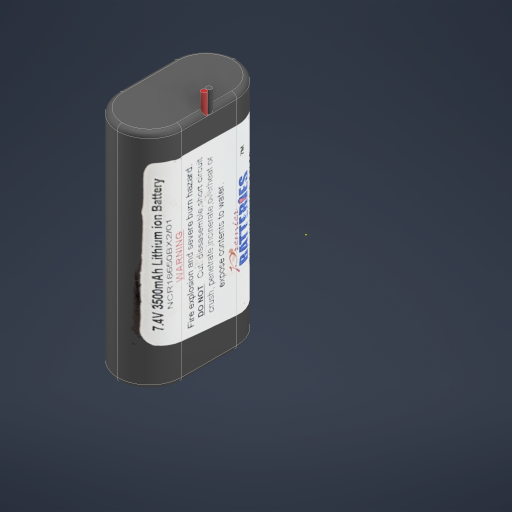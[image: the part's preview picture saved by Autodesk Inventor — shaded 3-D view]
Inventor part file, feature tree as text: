
AUTODESK INVENTOR PART (.ipt)
format: ipt  version: 2023 (Build 270158000, 158)  size: 811,008 bytes
history: native  units: mm
features: other x3, sketch x3, projected_geometry x2, extrude x1, boolean_combine x1, fillet x1, direct_edit x1, move_body x1
ambient origin geometry x8: Origin, YZ Plane, XZ Plane, XY Plane, X Axis, Y Axis, Z Axis, Center Point
bodies: Solid1 (feature_tree), Solid2 (feature_tree), Solid3 (feature_tree), Body1 (feature_tree), Body14 (feature_tree)
feature tree (13):
  extrude  "Extrusion1"  Depth=1.5mm
  boolean_combine  "Combine1"
  other  "Decal1"
  fillet  "Fillet1"  [1 undecoded]
  sketch  "Sketch3"
  direct_edit  "Direct Edit1"
  sketch  "Sketch1"  dims[d0=10.0mm d1=0.0mm d15=1.5mm]
  projected_geometry  "Projected Loop1"
  projected_geometry  "Projected Loop2"
  sketch  "Sketch2"  dims[d16=0.0mm d17=0.0mm d18=-1.5mm]
  other  "Image1"
  other  "Body14:1"
  move_body  "Move1"
note: 1 required parameter value undecoded (feature->parameter linkage not recoverable at this tier; creation-order binding heuristic only, values carry confidence <= 0.55)
